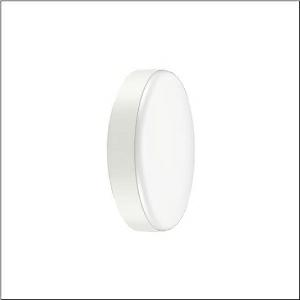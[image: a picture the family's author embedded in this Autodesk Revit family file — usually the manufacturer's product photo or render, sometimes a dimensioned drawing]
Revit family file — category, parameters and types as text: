
# Revit family: round_31_51wc10mb34as
name_source: partatom
category: Lighting Fixtures
units: mm (PartAtom-declared; Revit-internal decimal feet)

## family parameters
Cut with Voids When Loaded = No
Host = Face
Light Source = No
Part Type = Normal
Room Calculation Point = No
Round Connector Dimension = Use Diameter
Shared = No

## types (1)
- --- (1 x LED, 4250 lm, 35.4 W, 3000K)
    Apparent Load = 35 VA
    CIE Flux Codes = 44 75 94 94 100
    Color Rendering = 80
    Color Temperature = 3000K
    Default Elevation = 1800 mm
    Description = Round 31, wall and ceiling luminaire, primary optical cover: cover, of PC, opal, light emission: direct distribution, primary light characteristic: symmetric, installation type: surface-mounted, LED, rated luminous flux: 4.250lm, luminous efficacy: 120lm/W, light colour: 830, colour temperature: 3000K, control gear: ON/OFF Multilumen, with terminal, 3-pole, max. 2.5mm², mains connection: 220..240V, AC, 50/60Hz, rated input power: 35W, luminaire housing, of PC, traffic white (RAL 9016), diameter: 480mm, brightness and presence sensor, HF sensor, protection rating (complete): IP65, insulation class (complete): insulation class II (safety insulation), certification: CE, impact resistance: IK10, permissible operating ambient temperature: -20..+40°C, permissible storage temperature: -20..+60°C, packaging unit: 1 piece
    Height = 97 mm
    Lamp = 1 x LED
    Lamp Light Flux = 4250 lm
    Lamp Power = 35.4 W
    Lamp count = 1
    Length = 480 mm
    Luminous efficacy = 120 lm/W
    Manufacturer = Siteco
    ModVariant = No
    Model = 51WC10MB34AS
    Mounting Place = Ceiling
    Mounting Type = Surface mounted
    Number of Poles = 1
    OnlyDefault = Yes
    Power Factor = 1
    Product Name = Round 31
    Product group = wall and ceiling luminaire | ceiling mounted
    ProductGroupID = 305
    Protection Class = Protection class II
    Protection Degree = IP 65
    RLX_Detail_Level = 1
    RLX_Emergency_Light_Flux = 0 lm
    RLX_Emergency_Type = 0
    RLX_Emergency_Type_DB = No
    RlxData = <blob elided: 41445 chars, md5=e3c6e795>
    Socket = socket
    Standby Power = 0 W
    System Light Flux = 4250 lm
    System Power = 35 W
    Type Comments = factory setting: luminous flux: 100 % | (ON | ON)
    Type Image = l_1007188.jpg
    URL = http://relux.com
    VarID = @adj_133327
    Voltage = 0 V
    Weight = 0.00 kg
    Width = 0 mm  [stored 0 ft]

note: [stored X ft] marks values corroborated as IEEE doubles in the binary element streams (Revit-internal decimal feet)

## geometry (parser evidence)
native form markers: Blend x4, Sweep x10
no freeform markers — native parametric forms only
